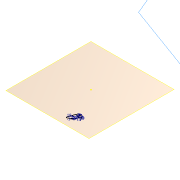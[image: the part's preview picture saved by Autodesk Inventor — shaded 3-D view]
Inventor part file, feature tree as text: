
AUTODESK INVENTOR PART (.ipt)
format: ipt  version: 2016 (Build 200138000, 138)  size: 165,376 bytes
history: native  units: mm
features: fillet x4, extrude x2, sketch x2, plane x1, reference x1, projected_geometry x1
ambient origin geometry x8: Origin, YZ Plane, XZ Plane, XY Plane, X Axis, Y Axis, Z Axis, Center Point
bodies: Solid1 (feature_tree)
feature tree (11):
  plane  "Work Plane1"
  extrude  "Extrusion1"  Depth=18.0mm
  extrude  "Extrusion2"  Depth=2.0mm
  fillet  "Fillet1"  Radius=5.0mm
  fillet  "Fillet2"  [1 undecoded]
  fillet  "Fillet3"  Radius=18.0mm
  fillet  "Fillet4"  Radius=8.0mm
  sketch  "Sketch1"  dims[d0=15.0mm d1=18.0mm]
  reference  "Reference1"
  sketch  "Sketch2"  dims[d2=18.0mm d3=8.726646mm d4=5.0mm d5=135.0deg d6=18.0mm d8=8.0mm d9=2.1mm d10=0.7mm d11=0.0mm d12=6.0mm d13=6.5mm d14=0.7mm d15=0.7mm d16=3.0mm d17=13.962634mm d18=135.0deg d19=13.5mm d20=0.0mm d21=1.0mm d22=14.0mm d23=5.0mm d24=0.5mm d25=0.5mm d26=2.0mm]
  projected_geometry  "Projected Loop1"
note: 1 required parameter value undecoded (feature->parameter linkage not recoverable at this tier; creation-order binding heuristic only, values carry confidence <= 0.55)
